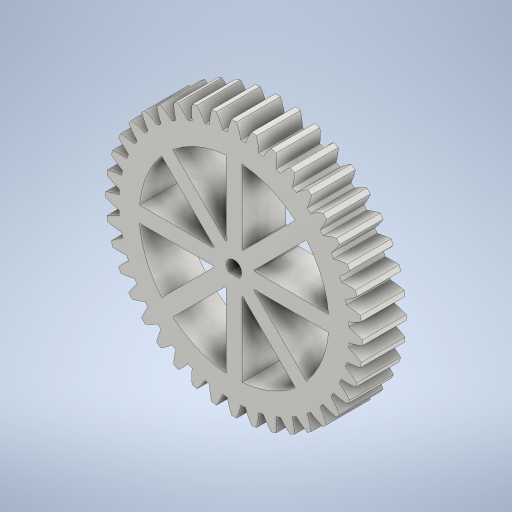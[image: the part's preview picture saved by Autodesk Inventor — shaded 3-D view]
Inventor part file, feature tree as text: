
AUTODESK INVENTOR PART (.ipt)
format: ipt  version: 2023 (Build 270158000, 158)  size: 1,122,816 bytes
history: native  units: mm (DEFAULTED — no unit token found)
features: sketch x4, extrude x3, plane x3, other x3
ambient origin geometry x8: Origin, YZ Plane, XZ Plane, XY Plane, X Axis, Y Axis, Z Axis, Center Point
bodies: Solid1 (feature_tree)
feature tree (13):
  extrude  "Extrusion1"  Depth=15.0mm TaperAngle=0.0deg
  plane  "Work Plane2"
  plane  "Work Plane8"
  plane  "Work Plane9"
  other  "Spur Gear"
  extrude  "Extrusion2"  Depth=10.0mm TaperAngle=0.0deg
  extrude  "Extrusion3"  Depth=0.785398mm TaperAngle=0.0deg
  sketch  "Sketch1"  dims[d0=88.0mm d1=15.0mm d2=0.0mm]
  sketch  "Sketch2"  dims[d3=80.0mm d4=10.0mm d5=0.0mm]
  other  "Srf1"
  sketch  "Sketch3"  dims[d16=200.0mm d17=0.0mm d34=0.785398mm]
  sketch  "Sketch4"  dims[d39=0.0mm d41=0.0mm d43=200.0mm d46=200.0mm d47=0.0mm d48=0.0mm d50=150.0mm d51=50.0mm d52=5.25mm d53=4.5mm d54=360.0deg d55=15.0mm d56=0.0mm d57=65.0mm d59=15.0mm d60=80.0mm d62=360.0deg d64=15.0mm d65=0.0mm]
  other  "Pitch Diameter"
